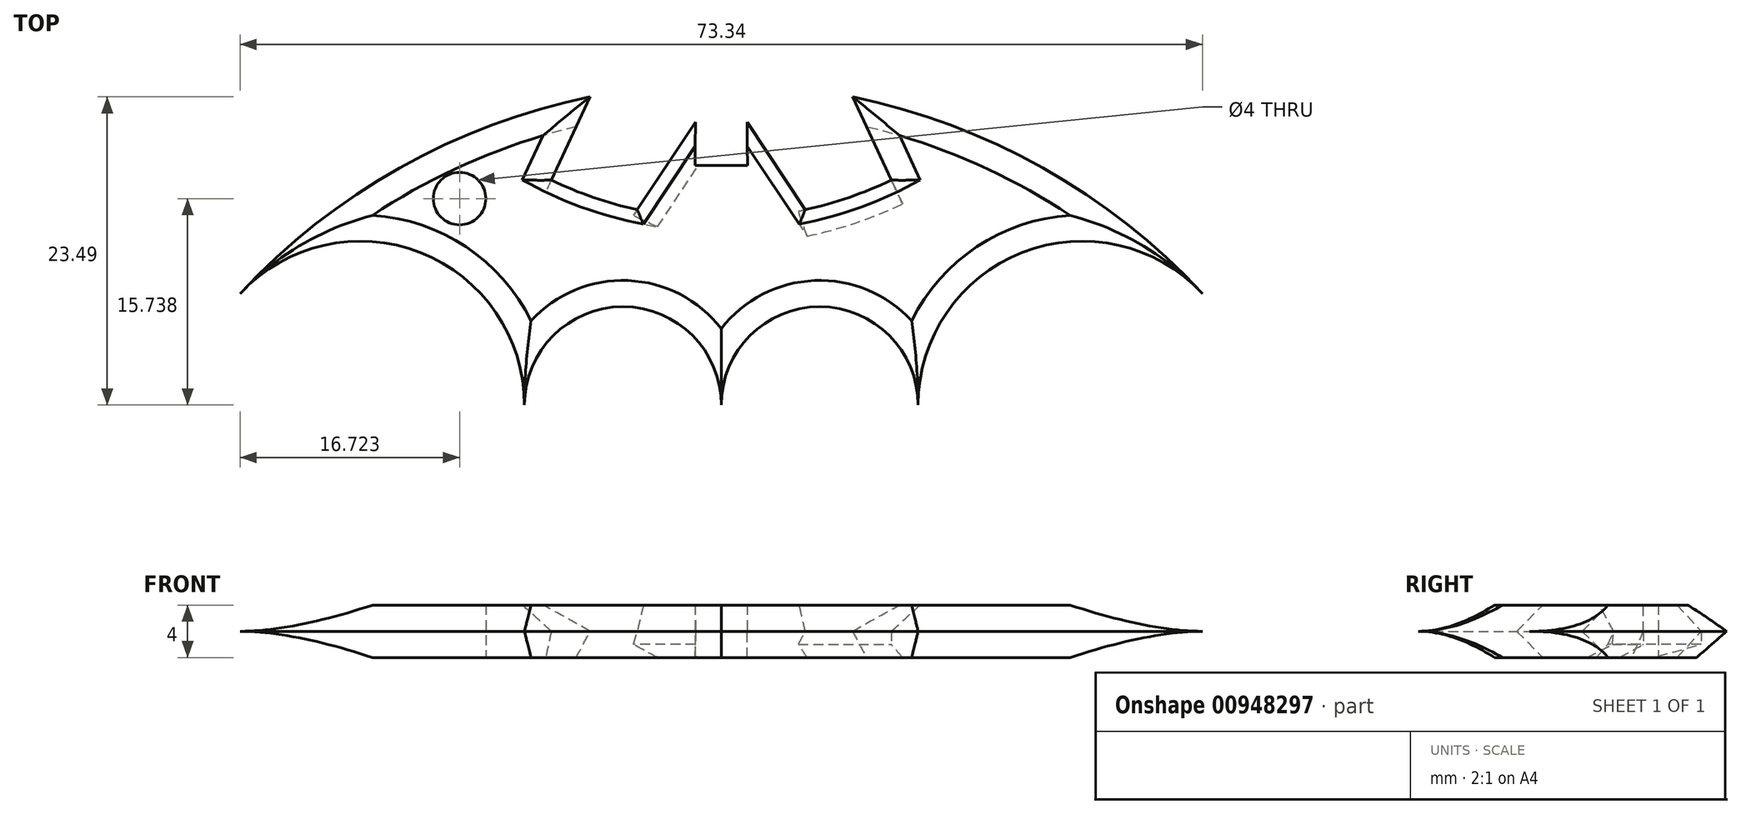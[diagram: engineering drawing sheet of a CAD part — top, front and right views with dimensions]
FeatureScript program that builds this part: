
annotation { "Feature Type Name" : "Feature", "Feature Type Description" : "" }
export const myFeature = defineFeature(function(context is Context, id is Id, definition is map)
    precondition{}
    {
        {
            var Q0;
            Q0=qCreatedBy(makeId("Top.planeOp"),FACE);
            var sketch = newSketch(context, id + "F0", { "sketchPlane" : qUnion([Q0])});
            skArc(sketch, "E0", {"start": v(-10, 48.99) * mm, "mid": v(-24.5, 43.58) * mm, "end": v(-36.67, 34) * mm});
            skLineSegment(sketch, "E1", {"start": v(-10, 48.99) * mm, "end": v(-12.96, 42.65) * mm});
            skLineSegment(sketch, "E2", {"start": v(10, 48.99) * mm, "end": v(12.96, 42.65) * mm});
            skArc(sketch, "E3", {"start": v(-12.96, 42.65) * mm, "mid": v(0, 39.7) * mm, "end": v(12.96, 42.65) * mm});
            skLineSegment(sketch, "E4", {"start": v(0, 0) * mm, "end": v(0, 50) * mm, "construction": true});
            skArc(sketch, "E5", {"start": v(-15, 25.5) * mm, "mid": v(-22.94, 37.13) * mm, "end": v(-36.67, 34) * mm});
            skArc(sketch, "E6", {"start": v(0, 25.5) * mm, "mid": v(-7.5, 33) * mm, "end": v(-15, 25.5) * mm});
            skLineSegment(sketch, "E7", {"start": v(-6.4, 40.4) * mm, "end": v(-1.97, 47.06) * mm});
            skLineSegment(sketch, "E8", {"start": v(-1.97, 47.06) * mm, "end": v(-2, 43.78) * mm});
            skLineSegment(sketch, "E9", {"start": v(-2, 43.78) * mm, "end": v(0, 43.78) * mm});
            skLineSegment(sketch, "E10.MirrorCS", {"start": v(6.4, 40.4) * mm, "end": v(1.97, 47.06) * mm});
            skLineSegment(sketch, "E11.MirrorCS", {"start": v(1.97, 47.06) * mm, "end": v(2, 43.78) * mm});
            skLineSegment(sketch, "E12.MirrorCS", {"start": v(2, 43.78) * mm, "end": v(0, 43.78) * mm});
            skArc(sketch, "E13.MirrorC", {"start": v(0, 25.5) * mm, "mid": v(7.5, 33) * mm, "end": v(15, 25.5) * mm});
            skArc(sketch, "E14.MirrorC", {"start": v(15, 25.5) * mm, "mid": v(22.94, 37.13) * mm, "end": v(36.67, 34) * mm});
            skCircle(sketch, "E15", {"center": v(-19.95, 41.24) * mm, "radius": 2 * mm});
            skArc(sketch, "E16.trimOffspring", {"start": v(36.67, 34) * mm, "mid": v(24.5, 43.58) * mm, "end": v(10, 48.99) * mm});
            skPoint(sketch, "E17", {"position": v(0, 25) * mm});
            skSolve(sketch);
        }
        {
            var Q0;
            Q0 = qSketchRegion(id + "F0", true);
            extrude(context, id + "F1", {"entities" : qUnion([Q0]), "depth" : 4 * mm, "offsetDistance" : 25 * mm});
        }
        {
            var Q0;
            Q0=makeQuery(id+"F1.opExtrude","CAP_EDGE",EDGE,{"disambiguationData":[OSD([sQuery(id+"F0.wireOp",EDGE,"E14.MirrorC")])],"isStart":false});
            var Q1;
            Q1=makeQuery(id+"F1.opExtrude","CAP_EDGE",EDGE,{"disambiguationData":[OSD([sQuery(id+"F0.wireOp",EDGE,"E13.MirrorC")])],"isStart":false});
            var Q2;
            Q2=makeQuery(id+"F1.opExtrude","CAP_EDGE",EDGE,{"disambiguationData":[OSD([sQuery(id+"F0.wireOp",EDGE,"E6")])],"isStart":false});
            var Q3;
            Q3=makeQuery(id+"F1.opExtrude","CAP_EDGE",EDGE,{"disambiguationData":[OSD([sQuery(id+"F0.wireOp",EDGE,"E5")])],"isStart":false});
            var Q4;
            Q4=makeQuery(id+"F1.opExtrude","CAP_EDGE",EDGE,{"disambiguationData":[OSD([sQuery(id+"F0.wireOp",EDGE,"E6")])],"isStart":true});
            var Q5;
            Q5=makeQuery(id+"F1.opExtrude","CAP_EDGE",EDGE,{"disambiguationData":[OSD([sQuery(id+"F0.wireOp",EDGE,"E13.MirrorC")])],"isStart":true});
            var Q6;
            Q6=makeQuery(id+"F1.opExtrude","CAP_EDGE",EDGE,{"disambiguationData":[OSD([sQuery(id+"F0.wireOp",EDGE,"E14.MirrorC")])],"isStart":true});
            var Q7;
            Q7=makeQuery(id+"F1.opExtrude","CAP_EDGE",EDGE,{"disambiguationData":[OSD([sQuery(id+"F0.wireOp",EDGE,"E5")])],"isStart":true});
            var Q8;
            Q8=makeQuery(id+"F1.opExtrude","CAP_EDGE",EDGE,{"disambiguationData":[OSD([sQuery(id+"F0.wireOp",EDGE,"E16.trimOffspring")])],"isStart":false});
            var Q9;
            Q9=makeQuery(id+"F1.opExtrude","CAP_EDGE",EDGE,{"disambiguationData":[OSD([sQuery(id+"F0.wireOp",EDGE,"E2")])],"isStart":false});
            var Q10;
            Q10=makeQuery(id+"F1.opExtrude","CAP_EDGE",EDGE,{"disambiguationData":[OSD([sQuery(id+"F0.wireOp",EDGE,"E1")])],"isStart":false});
            var Q11;
            Q11=makeQuery(id+"F1.opExtrude","CAP_EDGE",EDGE,{"disambiguationData":[OSD([sQuery(id+"F0.wireOp",EDGE,"E0")])],"isStart":false});
            var Q12;
            Q12=makeQuery(id+"F1.opExtrude","CAP_EDGE",EDGE,{"disambiguationData":[OSD([sQuery(id+"F0.wireOp",EDGE,"E0")])],"isStart":true});
            var Q13;
            Q13=makeQuery(id+"F1.opExtrude","CAP_EDGE",EDGE,{"disambiguationData":[OSD([sQuery(id+"F0.wireOp",EDGE,"E16.trimOffspring")])],"isStart":true});
            chamfer(context, id + "F2", {"entities" : qUnion([Q0, Q1, Q2, Q3, Q4, Q5, Q6, Q7, Q8, Q9, Q10, Q11, Q12, Q13]), "width" : 2 * mm, "tangentPropagation" : true});
        }
        {
            var Q0;
            {var subQ0=sQuery(id+"F0.wireOp",EDGE,"E3");Q0=makeQuery(id+"F1.opExtrude","CAP_EDGE",EDGE,{"disambiguationData":[OSD([subQ0]),TDD([makeQuery(id+"F0.imprint","IMPRINT",EDGE,{"disambiguationData":[TD([[makeQuery(id+"F0.imprint","INTERSECT",VERTEX,{"derivedFrom":[sQuery(id+"F0.wireOp",EDGE,"E1"),subQ0]}),-1.0]])],"derivedFrom":subQ0})])],"isStart":false});}
            var Q1;
            {var subQ0=sQuery(id+"F0.wireOp",EDGE,"E3");Q1=makeQuery(id+"F1.opExtrude","CAP_EDGE",EDGE,{"disambiguationData":[OSD([subQ0]),TDD([makeQuery(id+"F0.imprint","IMPRINT",EDGE,{"disambiguationData":[TD([[makeQuery(id+"F0.imprint","INTERSECT",VERTEX,{"derivedFrom":[sQuery(id+"F0.wireOp",EDGE,"E1"),subQ0]}),-1.0]])],"derivedFrom":subQ0})])],"isStart":true});}
            var Q2;
            {var subQ0=sQuery(id+"F0.wireOp",EDGE,"E3");Q2=makeQuery(id+"F1.opExtrude","CAP_EDGE",EDGE,{"disambiguationData":[OSD([subQ0]),TDD([makeQuery(id+"F0.imprint","IMPRINT",EDGE,{"disambiguationData":[TD([[makeQuery(id+"F0.imprint","INTERSECT",VERTEX,{"derivedFrom":[sQuery(id+"F0.wireOp",EDGE,"E2"),subQ0]}),1.0]])],"derivedFrom":subQ0})])],"isStart":false});}
            var Q3;
            {var subQ0=sQuery(id+"F0.wireOp",EDGE,"E3");Q3=makeQuery(id+"F1.opExtrude","CAP_EDGE",EDGE,{"disambiguationData":[OSD([subQ0]),TDD([makeQuery(id+"F0.imprint","IMPRINT",EDGE,{"disambiguationData":[TD([[makeQuery(id+"F0.imprint","INTERSECT",VERTEX,{"derivedFrom":[sQuery(id+"F0.wireOp",EDGE,"E2"),subQ0]}),1.0]])],"derivedFrom":subQ0})])],"isStart":true});}
            var Q4;
            Q4=makeQuery(id+"F1.opExtrude","CAP_EDGE",EDGE,{"disambiguationData":[OSD([sQuery(id+"F0.wireOp",EDGE,"E7")])],"isStart":false});
            var Q5;
            Q5=makeQuery(id+"F1.opExtrude","CAP_EDGE",EDGE,{"disambiguationData":[OSD([sQuery(id+"F0.wireOp",EDGE,"E7")])],"isStart":true});
            var Q6;
            Q6=makeQuery(id+"F1.opExtrude","CAP_EDGE",EDGE,{"disambiguationData":[OSD([sQuery(id+"F0.wireOp",EDGE,"E10.MirrorCS")])],"isStart":false});
            var Q7;
            Q7=makeQuery(id+"F1.opExtrude","CAP_EDGE",EDGE,{"disambiguationData":[OSD([sQuery(id+"F0.wireOp",EDGE,"E10.MirrorCS")])],"isStart":true});
            chamfer(context, id + "F3", {"entities" : qUnion([Q0, Q1, Q2, Q3, Q4, Q5, Q6, Q7]), "chamferType" : ChamferType.TWO_OFFSETS, "width1" : 2 * mm, "oppositeDirection" : false, "width2" : 1 * mm, "tangentPropagation" : true});
        }
    });
